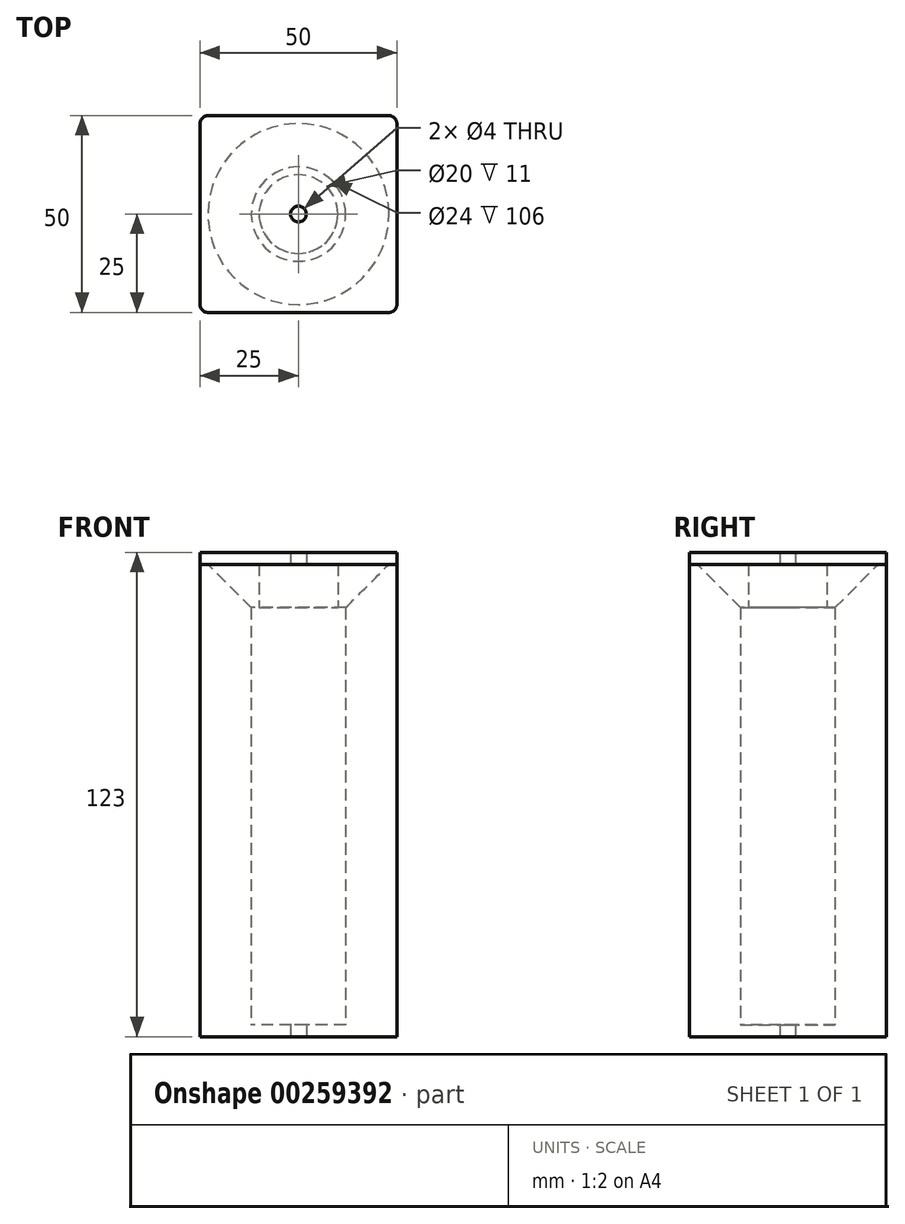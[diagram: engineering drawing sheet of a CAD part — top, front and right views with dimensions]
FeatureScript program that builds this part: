
annotation { "Feature Type Name" : "Feature", "Feature Type Description" : "" }
export const myFeature = defineFeature(function(context is Context, id is Id, definition is map)
    precondition{}
    {
        {
            var Q0;
            Q0=qCreatedBy(makeId("Top.planeOp"),FACE);
            var sketch = newSketch(context, id + "F0", { "sketchPlane" : qUnion([Q0])});
            skLineSegment(sketch, "E0.bottom", {"start": v(-25, 25) * mm, "end": v(25, 25) * mm});
            skLineSegment(sketch, "E0.top", {"start": v(-25, -25) * mm, "end": v(25, -25) * mm});
            skLineSegment(sketch, "E0.left", {"start": v(-25, 25) * mm, "end": v(-25, -25) * mm});
            skLineSegment(sketch, "E0.right", {"start": v(25, 25) * mm, "end": v(25, -25) * mm});
            skCircle(sketch, "E1", {"center": v(0, 0) * mm, "radius": 2 * mm});
            skCircle(sketch, "E2", {"center": v(0, 0) * mm, "radius": 12 * mm});
            skSolve(sketch);
        }
        {
            var Q0;
            Q0 = qSketchRegion(id + "F0", true);
            extrude(context, id + "F1", {"entities" : qUnion([Q0]), "depth" : 120 * mm, "offsetDistance" : 25 * mm});
        }
        {
            var Q0;
            Q0=makeQuery(id+"F0.imprint","IMPRINT",FACE,{"disambiguationData":[TD([[makeQuery(id+"F0.imprint","IMPRINT",EDGE,{"derivedFrom":sQuery(id+"F0.wireOp",EDGE,"E1")}),-1.0]])]});
            extrude(context, id + "F2", {"entities" : qUnion([Q0]), "operationType" : NewBodyOperationType.ADD, "depth" : 3 * mm, "offsetDistance" : 25 * mm});
        }
        {
            var Q0;
            Q0=makeQuery(id+"F1.opExtrude","CAP_EDGE",EDGE,{"disambiguationData":[OSD([sQuery(id+"F0.wireOp",EDGE,"Tpu84ZZH-03Ez-Z0EC-sTv4-LuyJvKzuljnh.left")])],"isStart":false});
            var Q1;
            Q1=makeQuery(id+"F1.opExtrude","CAP_EDGE",EDGE,{"disambiguationData":[OSD([sQuery(id+"F0.wireOp",EDGE,"Tpu84ZZH-03Ez-Z0EC-sTv4-LuyJvKzuljnh.top")])],"isStart":false});
            var Q2;
            Q2=makeQuery(id+"F1.opExtrude","CAP_EDGE",EDGE,{"disambiguationData":[OSD([sQuery(id+"F0.wireOp",EDGE,"Tpu84ZZH-03Ez-Z0EC-sTv4-LuyJvKzuljnh.right")])],"isStart":false});
            var Q3;
            Q3=makeQuery(id+"F1.opExtrude","CAP_EDGE",EDGE,{"disambiguationData":[OSD([sQuery(id+"F0.wireOp",EDGE,"Tpu84ZZH-03Ez-Z0EC-sTv4-LuyJvKzuljnh.bottom")])],"isStart":false});
            var Q4;
            Q4=makeQuery(id+"F1.opExtrude","CAP_EDGE",EDGE,{"disambiguationData":[OSD([sQuery(id+"F0.wireOp",EDGE,"E2")])],"isStart":false});
            chamfer(context, id + "F3", {"entities" : qUnion([Q0, Q1, Q2, Q3, Q4]), "width" : 11 * mm, "tangentPropagation" : true});
        }
        {
            var Q0;
            Q0=makeQuery(id+"F1.opExtrude","CAP_FACE",FACE,{"disambiguationData":[OSD([sQuery(id+"F0.wireOp",EDGE,"E0.bottom"),sQuery(id+"F0.wireOp",EDGE,"E0.top"),sQuery(id+"F0.wireOp",EDGE,"E0.left"),sQuery(id+"F0.wireOp",EDGE,"E0.right"),sQuery(id+"F0.wireOp",EDGE,"Tpu84ZZH-03Ez-Z0EC-sTv4-LuyJvKzuljnh.bottom"),sQuery(id+"F0.wireOp",EDGE,"Tpu84ZZH-03Ez-Z0EC-sTv4-LuyJvKzuljnh.top"),sQuery(id+"F0.wireOp",EDGE,"Tpu84ZZH-03Ez-Z0EC-sTv4-LuyJvKzuljnh.left"),sQuery(id+"F0.wireOp",EDGE,"Tpu84ZZH-03Ez-Z0EC-sTv4-LuyJvKzuljnh.right")])],"isStart":false});
            var sketch = newSketch(context, id + "F4", { "sketchPlane" : qUnion([Q0])});
            skLineSegment(sketch, "E3.0", {"start": v(-25, -25) * mm, "end": v(25, -25) * mm});
            skLineSegment(sketch, "E3.1", {"start": v(25, 25) * mm, "end": v(25, -25) * mm});
            skLineSegment(sketch, "E3.2", {"start": v(-25, 25) * mm, "end": v(25, 25) * mm});
            skLineSegment(sketch, "E3.3", {"start": v(-25, 25) * mm, "end": v(-25, -25) * mm});
            skCircle(sketch, "E4.0", {"center": v(0, 0) * mm, "radius": 2 * mm});
            skSolve(sketch);
        }
        {
            var Q0;
            Q0 = qSketchRegion(id + "F4", true);
            extrude(context, id + "F5", {"entities" : qUnion([Q0]), "depth" : 3 * mm, "offsetDistance" : 25 * mm, "hasSecondDirection" : true, "secondDirectionOppositeDirection" : true, "secondDirectionDepth" : 11 * mm});
        }
        {
            var Q0;
            Q0=makeQuery(id+"F1.opExtrude","SWEPT_BODY",BODY,{"disambiguationData":[OSD([sQuery(id+"F0.wireOp",EDGE,"E0.bottom"),sQuery(id+"F0.wireOp",EDGE,"E0.top"),sQuery(id+"F0.wireOp",EDGE,"E0.left"),sQuery(id+"F0.wireOp",EDGE,"E0.right"),sQuery(id+"F0.wireOp",EDGE,"Tpu84ZZH-03Ez-Z0EC-sTv4-LuyJvKzuljnh.bottom"),sQuery(id+"F0.wireOp",EDGE,"Tpu84ZZH-03Ez-Z0EC-sTv4-LuyJvKzuljnh.top"),sQuery(id+"F0.wireOp",EDGE,"Tpu84ZZH-03Ez-Z0EC-sTv4-LuyJvKzuljnh.left"),sQuery(id+"F0.wireOp",EDGE,"Tpu84ZZH-03Ez-Z0EC-sTv4-LuyJvKzuljnh.right")])]});
            var Q1;
            Q1=makeQuery(id+"F5.opExtrude","SWEPT_BODY",BODY,{"disambiguationData":[OSD([sQuery(id+"F4.wireOp",EDGE,"E3.0"),sQuery(id+"F4.wireOp",EDGE,"E3.1"),sQuery(id+"F4.wireOp",EDGE,"E3.2"),sQuery(id+"F4.wireOp",EDGE,"E3.3")])]});
            booleanBodies(context, id + "F6", {"operationType" : BooleanOperationType.SUBTRACTION, "tools" : qUnion([Q0]), "targets" : qUnion([Q1]), "keepTools" : true});
        }
        {
            var Q0;
            Q0=makeQuery(id+"F5.opExtrude","CAP_FACE",FACE,{"disambiguationData":[OSD([sQuery(id+"F4.wireOp",EDGE,"E3.0"),sQuery(id+"F4.wireOp",EDGE,"E3.1"),sQuery(id+"F4.wireOp",EDGE,"E3.2"),sQuery(id+"F4.wireOp",EDGE,"E3.3"),sQuery(id+"F4.wireOp",EDGE,"E4.0")])],"isStart":true});
            var sketch = newSketch(context, id + "F7", { "sketchPlane" : qUnion([Q0])});
            skCircle(sketch, "E5", {"center": v(0, 0) * mm, "radius": 10 * mm});
            skSolve(sketch);
        }
        {
            var Q0;
            Q0 = qSketchRegion(id + "F7", true);
            var Q1;
            Q1=makeQuery(id+"F6.opBoolean","COPY",FACE,{"derivedFrom":makeQuery(id+"F1.opExtrude","CAP_FACE",FACE,{"disambiguationData":[OSD([sQuery(id+"F0.wireOp",EDGE,"E0.bottom"),sQuery(id+"F0.wireOp",EDGE,"E0.top"),sQuery(id+"F0.wireOp",EDGE,"E0.left"),sQuery(id+"F0.wireOp",EDGE,"E0.right"),sQuery(id+"F0.wireOp",EDGE,"E2")])],"isStart":false})});
            extrude(context, id + "F8", {"entities" : qUnion([Q0]), "operationType" : NewBodyOperationType.REMOVE, "endBound" : BoundingType.UP_TO_SURFACE, "oppositeDirection" : true, "depth" : 25 * mm, "endBoundEntityFace" : qUnion([Q1]), "offsetDistance" : 25 * mm});
        }
        {
            var Q0;
            Q0=makeQuery(id+"F1.opExtrude","SWEPT_EDGE",EDGE,{"disambiguationData":[OSD([sQuery(id+"F0.wireOp",EDGE,"E0.top"),sQuery(id+"F0.wireOp",EDGE,"E0.right")])]});
            var Q1;
            Q1=makeQuery(id+"F5.opExtrude","SWEPT_EDGE",EDGE,{"disambiguationData":[OSD([sQuery(id+"F4.wireOp",EDGE,"E3.0"),sQuery(id+"F4.wireOp",EDGE,"E3.1")])]});
            var Q2;
            Q2=makeQuery(id+"F5.opExtrude","SWEPT_EDGE",EDGE,{"disambiguationData":[OSD([sQuery(id+"F4.wireOp",EDGE,"E3.1"),sQuery(id+"F4.wireOp",EDGE,"E3.2")])]});
            var Q3;
            Q3=makeQuery(id+"F1.opExtrude","SWEPT_EDGE",EDGE,{"disambiguationData":[OSD([sQuery(id+"F0.wireOp",EDGE,"E0.bottom"),sQuery(id+"F0.wireOp",EDGE,"E0.right")])]});
            var Q4;
            Q4=makeQuery(id+"F5.opExtrude","SWEPT_EDGE",EDGE,{"disambiguationData":[OSD([sQuery(id+"F4.wireOp",EDGE,"E3.2"),sQuery(id+"F4.wireOp",EDGE,"E3.3")])]});
            var Q5;
            Q5=makeQuery(id+"F1.opExtrude","SWEPT_EDGE",EDGE,{"disambiguationData":[OSD([sQuery(id+"F0.wireOp",EDGE,"E0.bottom"),sQuery(id+"F0.wireOp",EDGE,"E0.left")])]});
            var Q6;
            Q6=makeQuery(id+"F5.opExtrude","SWEPT_EDGE",EDGE,{"disambiguationData":[OSD([sQuery(id+"F4.wireOp",EDGE,"E3.0"),sQuery(id+"F4.wireOp",EDGE,"E3.3")])]});
            var Q7;
            Q7=makeQuery(id+"F1.opExtrude","SWEPT_EDGE",EDGE,{"disambiguationData":[OSD([sQuery(id+"F0.wireOp",EDGE,"E0.top"),sQuery(id+"F0.wireOp",EDGE,"E0.left")])]});
            fillet(context, id + "F9", {"entities" : qUnion([Q0, Q1, Q2, Q3, Q4, Q5, Q6, Q7]), "tangentPropagation" : true, "radius" : 2 * mm, "defaultsChanged" : true, "vertexSettings" : [], "allowEdgeOverflow" : false});
        }
    });
